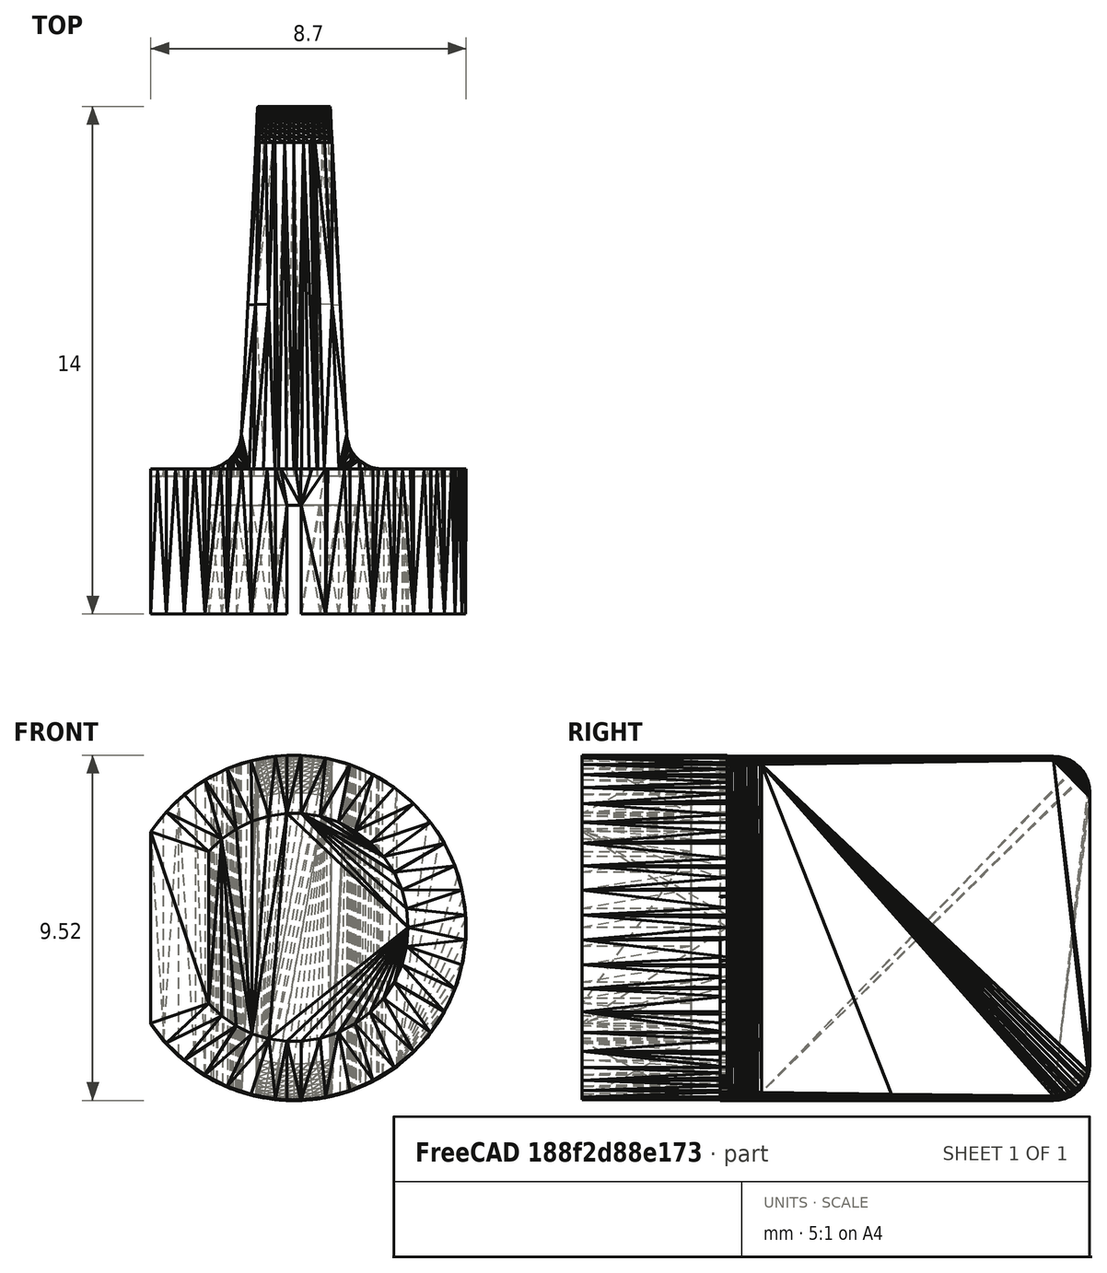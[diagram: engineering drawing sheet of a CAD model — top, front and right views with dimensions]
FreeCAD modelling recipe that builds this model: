
FCSTD DOCUMENT  (FreeCAD 1.0R39319 (Git))
Label: TheThing_v8-trimpot_knob
License: CERN Open Hardware Licence permissive
LicenseURL: https://cern-ohl.web.cern.ch/
objects: Mesh::Feature×2, Part::Feature×2, Part::Box×2, Part::Cut×2
note: 6 computed .brp shape members not serialized (recipe doc carries the construction recipe); baked Part::Feature solids carry a one-line shape summary decoded from their .brp

FEATURE [Mesh::Feature] Knob8
FEATURE [Mesh::Feature] Slot1
  Placement = pos=(-2.6,0,-4.2) rot=(0,0,1;0rad)
FEATURE [Part::Feature] Knob009
  shape: bbox 8.691 x 14 x 9.5 mm, 1172 faces, 0 solids (baked)
FEATURE [Part::Feature] Slot002
  shape: bbox 13 x 16 x 13 mm, 1832 faces, 0 solids (baked)
FEATURE [Part::Box] Box  label="Cube"
  AttacherType = Attacher::AttachEngine3D
  Height = 16
  Length = 15
  Placement = pos=(-4,4,-4) rot=(0,0,1;0rad)
  Width = 16
FEATURE [Part::Cut] Cut
  Base = -> Slot002
  Refine = true
  Tool = -> Box
FEATURE [Part::Box] Box001  label="Cube001"
  AttacherType = Attacher::AttachEngine3D
  Height = 10
  Length = 10
  Placement = pos=(-1,-6.2,0) rot=(0,0,1;0rad)
  Width = 10
FEATURE [Part::Cut] Cut001
  Base = -> Knob009
  Refine = true
  Tool = -> Box001
